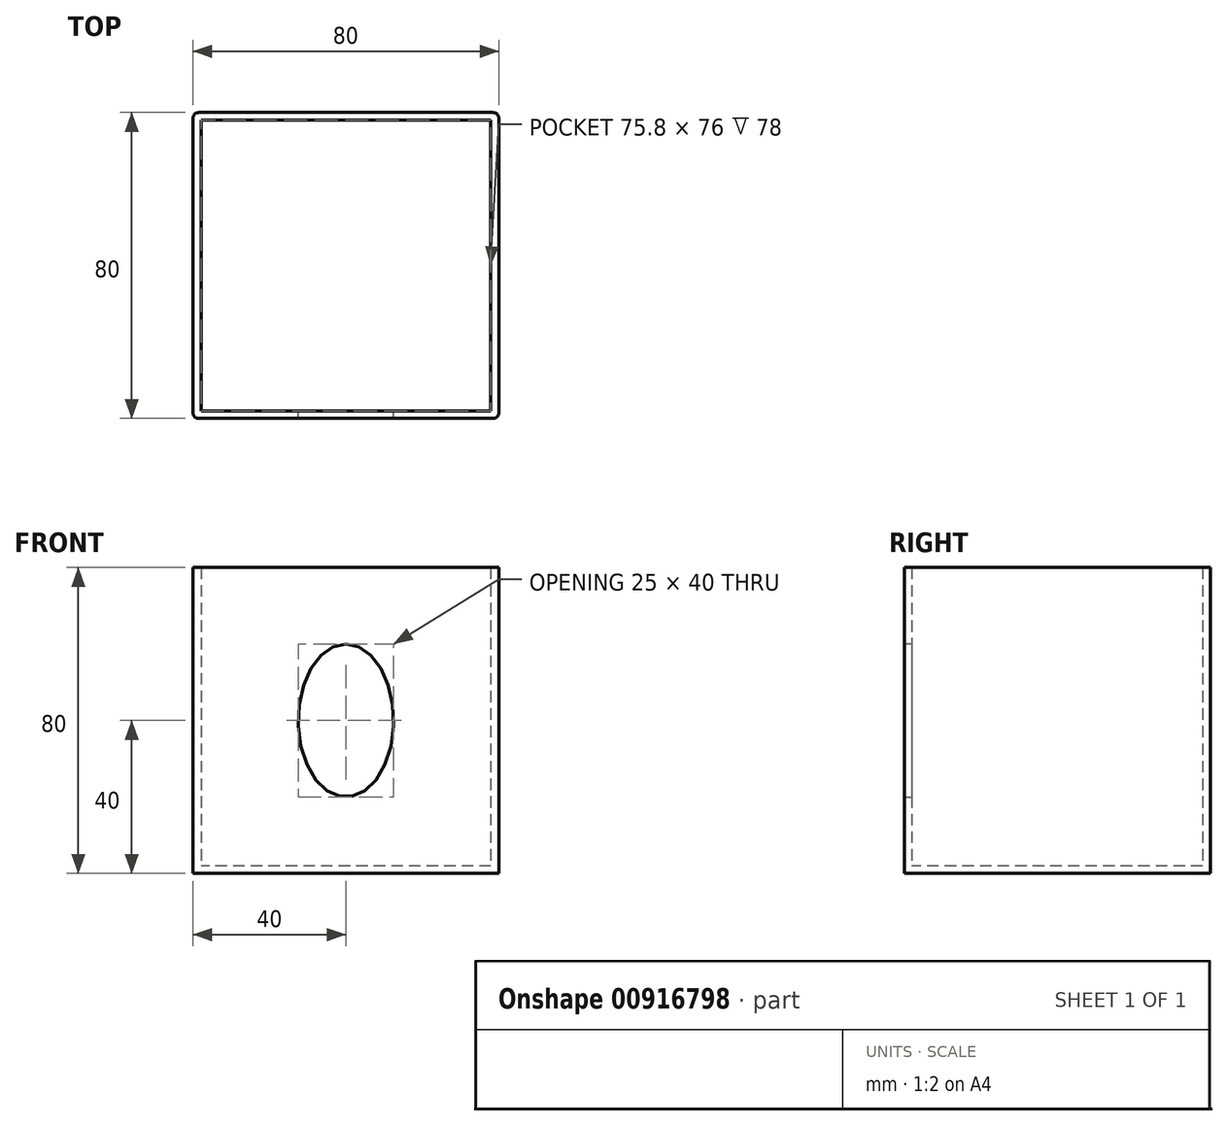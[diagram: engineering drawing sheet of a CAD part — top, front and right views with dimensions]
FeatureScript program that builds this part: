
annotation { "Feature Type Name" : "Feature", "Feature Type Description" : "" }
export const myFeature = defineFeature(function(context is Context, id is Id, definition is map)
    precondition{}
    {
        {
            var Q0;
            Q0=qCreatedBy(makeId("Top.planeOp"),FACE);
            var sketch = newSketch(context, id + "F0", { "sketchPlane" : qUnion([Q0])});
            skLineSegment(sketch, "E0.bottom", {"start": v(40, 40) * mm, "end": v(-40, 40) * mm});
            skLineSegment(sketch, "E0.top", {"start": v(40, -40) * mm, "end": v(-40, -40) * mm});
            skLineSegment(sketch, "E0.left", {"start": v(40, 40) * mm, "end": v(40, -40) * mm});
            skLineSegment(sketch, "E0.right", {"start": v(-40, 40) * mm, "end": v(-40, -40) * mm});
            skPoint(sketch, "E0.middle", {"position": v(0, 0) * mm});
            skLineSegment(sketch, "E1.bottom", {"start": v(37.9, 38) * mm, "end": v(-37.9, 38) * mm});
            skLineSegment(sketch, "E1.top", {"start": v(37.9, -38) * mm, "end": v(-37.9, -38) * mm});
            skLineSegment(sketch, "E1.left", {"start": v(37.9, 38) * mm, "end": v(37.9, -38) * mm});
            skLineSegment(sketch, "E1.right", {"start": v(-37.9, 38) * mm, "end": v(-37.9, -38) * mm});
            skSolve(sketch);
        }
        {
            var Q0;
            Q0=makeQuery(id+"F0.imprint","IMPRINT",FACE,{"disambiguationData":[TD([[makeQuery(id+"F0.imprint","IMPRINT",EDGE,{"derivedFrom":sQuery(id+"F0.wireOp",EDGE,"E0.bottom")}),1.0]])]});
            extrude(context, id + "F1", {"entities" : qUnion([Q0]), "depth" : 80 * mm, "offsetDistance" : 25 * mm});
        }
        {
            var Q0;
            Q0=makeQuery(id+"F0.imprint","IMPRINT",FACE,{"disambiguationData":[TD([[makeQuery(id+"F0.imprint","IMPRINT",EDGE,{"derivedFrom":sQuery(id+"F0.wireOp",EDGE,"E1.bottom")}),1.0]])]});
            extrude(context, id + "F2", {"entities" : qUnion([Q0]), "operationType" : NewBodyOperationType.ADD, "depth" : 2 * mm, "offsetDistance" : 25 * mm});
        }
        {
            var Q0;
            Q0=makeQuery(id+"F1.opExtrude","SWEPT_FACE",FACE,{"disambiguationData":[OSD([sQuery(id+"F0.wireOp",EDGE,"E0.top")])]});
            var sketch = newSketch(context, id + "F3", { "sketchPlane" : qUnion([Q0])});
            skLineSegment(sketch, "E2", {"start": v(0, 80) * mm, "end": v(0, 0) * mm});
            skLineSegment(sketch, "E3", {"start": v(-40, 40) * mm, "end": v(40, 40) * mm});
            skEllipse(sketch, "E4", {"center": v(0, 40) * mm, "majorRadius": 20 * mm, "minorRadius": 12.5 * mm, "majorAxis": v(0, 1)});
            skSolve(sketch);
        }
        {
            var Q0;
            {var subQ0=sQuery(id+"F3.wireOp",EDGE,"E4");var subQ1=sQuery(id+"F3.wireOp",EDGE,"E2");var subQ2=makeQuery(id+"F3.imprint","INTERSECT",VERTEX,{"disambiguationData":[OD(0.0)],"derivedFrom":[subQ1,subQ0]});Q0=makeQuery(id+"F3.imprint","IMPRINT",FACE,{"disambiguationData":[TD([[makeQuery(id+"F3.imprint","IMPRINT",EDGE,{"disambiguationData":[TD([[subQ2,-1.0]])],"derivedFrom":subQ1}),-1.0]])]});}
            var Q1;
            {var subQ0=sQuery(id+"F3.wireOp",EDGE,"E4");var subQ1=sQuery(id+"F3.wireOp",EDGE,"E2");var subQ2=makeQuery(id+"F3.imprint","INTERSECT",VERTEX,{"disambiguationData":[OD(0.0)],"derivedFrom":[subQ1,subQ0]});Q1=makeQuery(id+"F3.imprint","IMPRINT",FACE,{"disambiguationData":[TD([[makeQuery(id+"F3.imprint","IMPRINT",EDGE,{"disambiguationData":[TD([[subQ2,-1.0]])],"derivedFrom":subQ1}),1.0]])]});}
            var Q2;
            {var subQ0=sQuery(id+"F3.wireOp",EDGE,"E3");var subQ1=sQuery(id+"F3.wireOp",EDGE,"E2");var subQ2=makeQuery(id+"F3.imprint","INTERSECT",VERTEX,{"derivedFrom":[subQ1,subQ0]});Q2=makeQuery(id+"F3.imprint","IMPRINT",FACE,{"disambiguationData":[TD([[makeQuery(id+"F3.imprint","IMPRINT",EDGE,{"disambiguationData":[TD([[subQ2,-1.0]])],"derivedFrom":subQ1}),1.0]])]});}
            var Q3;
            {var subQ0=sQuery(id+"F3.wireOp",EDGE,"E3");var subQ1=sQuery(id+"F3.wireOp",EDGE,"E2");var subQ2=makeQuery(id+"F3.imprint","INTERSECT",VERTEX,{"derivedFrom":[subQ1,subQ0]});Q3=makeQuery(id+"F3.imprint","IMPRINT",FACE,{"disambiguationData":[TD([[makeQuery(id+"F3.imprint","IMPRINT",EDGE,{"disambiguationData":[TD([[subQ2,-1.0]])],"derivedFrom":subQ1}),-1.0]])]});}
            extrude(context, id + "F4", {"entities" : qUnion([Q0, Q1, Q2, Q3]), "operationType" : NewBodyOperationType.REMOVE, "oppositeDirection" : true, "depth" : 25 * mm, "offsetDistance" : 25 * mm});
        }
        {
            var Q0;
            Q0=makeQuery(id+"F1.opExtrude","SWEPT_EDGE",EDGE,{"disambiguationData":[OSD([sQuery(id+"F0.wireOp",EDGE,"E0.top"),sQuery(id+"F0.wireOp",EDGE,"E0.right")])]});
            var Q1;
            Q1=makeQuery(id+"F1.opExtrude","SWEPT_EDGE",EDGE,{"disambiguationData":[OSD([sQuery(id+"F0.wireOp",EDGE,"E0.bottom"),sQuery(id+"F0.wireOp",EDGE,"E0.left")])]});
            var Q2;
            Q2=makeQuery(id+"F1.opExtrude","SWEPT_EDGE",EDGE,{"disambiguationData":[OSD([sQuery(id+"F0.wireOp",EDGE,"E0.bottom"),sQuery(id+"F0.wireOp",EDGE,"E0.right")])]});
            var Q3;
            Q3=makeQuery(id+"FNIgZZU2rtYuzzn_1.boolean.opBoolean","MERGE",EDGE,{"derivedFrom":[makeQuery(id+"FZfziQPHYmBFav8_1.opExtrude","CAP_EDGE",EDGE,{"disambiguationData":[OSD([sQuery(id+"FbeFg03qAOgEDsT_1.wireOp",EDGE,"R9PmjM3O-VniN-3JSu-GzrK-uE917jMHUs6H.bottom")])],"isStart":false}),makeQuery(id+"FNIgZZU2rtYuzzn_1.opExtrude","SWEPT_EDGE",EDGE,{"disambiguationData":[OSD([sQuery(id+"Fgp7JZ7tiEEtYBI_1.wireOp",EDGE,"Cq0dyVJE-ZQKw-BNwl-LRCb-3fNCKQdDYhHc.bottom"),sQuery(id+"Fgp7JZ7tiEEtYBI_1.wireOp",EDGE,"Cq0dyVJE-ZQKw-BNwl-LRCb-3fNCKQdDYhHc.right")])]})]});
            var Q4;
            Q4=makeQuery(id+"FNIgZZU2rtYuzzn_1.boolean.opBoolean","MERGE",EDGE,{"derivedFrom":[makeQuery(id+"FZfziQPHYmBFav8_1.opExtrude","CAP_EDGE",EDGE,{"disambiguationData":[OSD([sQuery(id+"FbeFg03qAOgEDsT_1.wireOp",EDGE,"R9PmjM3O-VniN-3JSu-GzrK-uE917jMHUs6H.top")])],"isStart":false}),makeQuery(id+"FNIgZZU2rtYuzzn_1.opExtrude","SWEPT_EDGE",EDGE,{"disambiguationData":[OSD([sQuery(id+"Fgp7JZ7tiEEtYBI_1.wireOp",EDGE,"Cq0dyVJE-ZQKw-BNwl-LRCb-3fNCKQdDYhHc.bottom"),sQuery(id+"Fgp7JZ7tiEEtYBI_1.wireOp",EDGE,"Cq0dyVJE-ZQKw-BNwl-LRCb-3fNCKQdDYhHc.left")])]})]});
            var Q5;
            Q5=makeQuery(id+"F3BDCHb9nRchuBw_1.boolean.opBoolean","MERGE",EDGE,{"derivedFrom":[makeQuery(id+"FZfziQPHYmBFav8_1.opExtrude","CAP_EDGE",EDGE,{"disambiguationData":[OSD([sQuery(id+"FbeFg03qAOgEDsT_1.wireOp",EDGE,"b26fc71a-3270-4d3d-89a5-59d6ef7e8832.1.0.0")])],"isStart":false}),makeQuery(id+"F3BDCHb9nRchuBw_1.opExtrude","SWEPT_EDGE",EDGE,{"disambiguationData":[OSD([sQuery(id+"FleFPdL2fBdPsby_1.wireOp",EDGE,"2XgbG8Pz-ij24-29Ag-fRcY-cs6PM0wxYn33.bottom"),sQuery(id+"FleFPdL2fBdPsby_1.wireOp",EDGE,"2XgbG8Pz-ij24-29Ag-fRcY-cs6PM0wxYn33.left")])]})]});
            var Q6;
            Q6=makeQuery(id+"F3BDCHb9nRchuBw_1.boolean.opBoolean","MERGE",EDGE,{"derivedFrom":[makeQuery(id+"FZfziQPHYmBFav8_1.opExtrude","CAP_EDGE",EDGE,{"disambiguationData":[OSD([sQuery(id+"FbeFg03qAOgEDsT_1.wireOp",EDGE,"b26fc71a-3270-4d3d-89a5-59d6ef7e8832.1.0.3")])],"isStart":false}),makeQuery(id+"F3BDCHb9nRchuBw_1.opExtrude","SWEPT_EDGE",EDGE,{"disambiguationData":[OSD([sQuery(id+"FleFPdL2fBdPsby_1.wireOp",EDGE,"2XgbG8Pz-ij24-29Ag-fRcY-cs6PM0wxYn33.bottom"),sQuery(id+"FleFPdL2fBdPsby_1.wireOp",EDGE,"2XgbG8Pz-ij24-29Ag-fRcY-cs6PM0wxYn33.right")])]})]});
            var Q7;
            Q7=makeQuery(id+"F3BDCHb9nRchuBw_1.opExtrude","CAP_EDGE",EDGE,{"disambiguationData":[OSD([sQuery(id+"FleFPdL2fBdPsby_1.wireOp",EDGE,"2XgbG8Pz-ij24-29Ag-fRcY-cs6PM0wxYn33.bottom")])],"isStart":false});
            var Q8;
            Q8=makeQuery(id+"FNIgZZU2rtYuzzn_1.opExtrude","CAP_EDGE",EDGE,{"disambiguationData":[OSD([sQuery(id+"Fgp7JZ7tiEEtYBI_1.wireOp",EDGE,"Cq0dyVJE-ZQKw-BNwl-LRCb-3fNCKQdDYhHc.bottom")])],"isStart":false});
            var Q9;
            Q9=makeQuery(id+"F1.opExtrude","SWEPT_EDGE",EDGE,{"disambiguationData":[OSD([sQuery(id+"F0.wireOp",EDGE,"E0.top"),sQuery(id+"F0.wireOp",EDGE,"E0.left")])]});
            fillet(context, id + "F5", {"entities" : qUnion([Q0, Q1, Q2, Q3, Q4, Q5, Q6, Q7, Q8, Q9]), "radius" : 1.5 * mm, "tangentPropagation" : true, "allowEdgeOverflow" : false});
        }
    });
